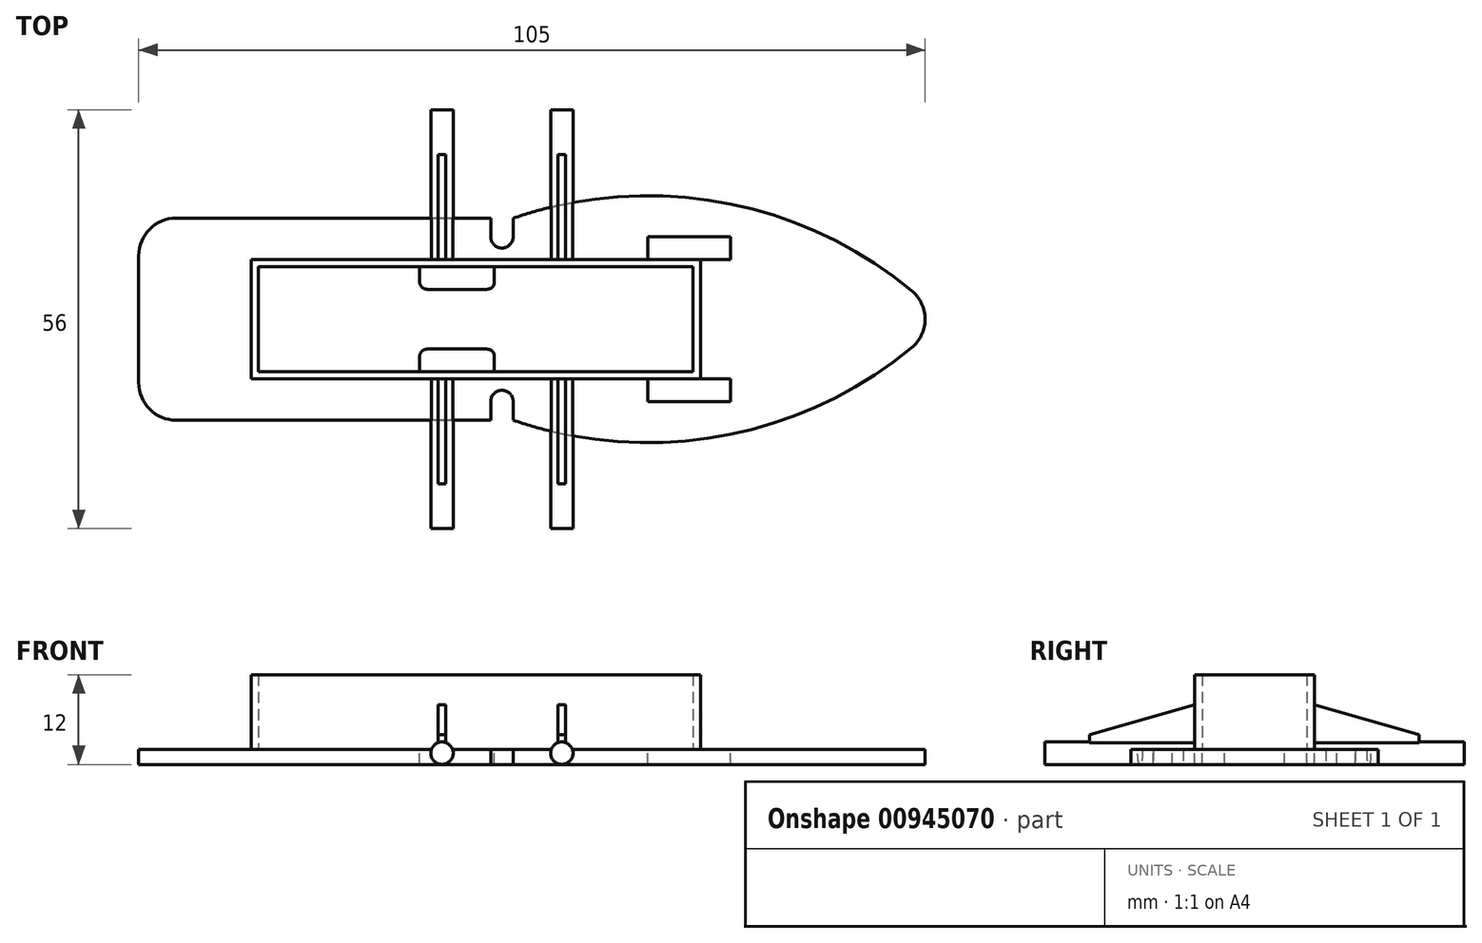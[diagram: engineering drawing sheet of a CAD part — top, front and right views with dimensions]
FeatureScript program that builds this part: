
annotation { "Feature Type Name" : "Feature", "Feature Type Description" : "" }
export const myFeature = defineFeature(function(context is Context, id is Id, definition is map)
    precondition{}
    {
        {
            var Q0;
            Q0=qCreatedBy(makeId("Top.planeOp"),FACE);
            var sketch = newSketch(context, id + "F0", { "sketchPlane" : qUnion([Q0])});
            skLineSegment(sketch, "E0", {"start": v(-48.5, 0) * mm, "end": v(-48.5, 8.5) * mm});
            skLineSegment(sketch, "E1", {"start": v(-43.5, 13.5) * mm, "end": v(-1.5, 13.5) * mm});
            skLineSegment(sketch, "E2", {"start": v(-1.5, 13.5) * mm, "end": v(-1.5, 11) * mm});
            skLineSegment(sketch, "E3", {"start": v(1.5, 11) * mm, "end": v(1.5, 13.5) * mm});
            skArc(sketch, "E4", {"start": v(54.68, 3.86) * mm, "mid": v(29.35, 15.61) * mm, "end": v(1.5, 13.5) * mm});
            skArc(sketch, "E5", {"start": v(-1.5, 11) * mm, "mid": v(0, 9.5) * mm, "end": v(1.5, 11) * mm});
            skPoint(sketch, "E6.visualSharp", {"position": v(-48.5, 13.5) * mm});
            skArc(sketch, "E6.filletArc", {"start": v(-43.5, 13.5) * mm, "mid": v(-47.04, 12.04) * mm, "end": v(-48.5, 8.5) * mm});
            skLineSegment(sketch, "E7.MirrorCS", {"start": v(1.5, -11) * mm, "end": v(1.5, -13.5) * mm});
            skLineSegment(sketch, "E8.MirrorCS", {"start": v(-1.5, -13.5) * mm, "end": v(-1.5, -11) * mm});
            skArc(sketch, "E9.MirrorCS", {"start": v(-43.5, -13.5) * mm, "mid": v(-47.04, -12.04) * mm, "end": v(-48.5, -8.5) * mm});
            skArc(sketch, "E10.MirrorCS", {"start": v(-1.5, -11) * mm, "mid": v(0, -9.5) * mm, "end": v(1.5, -11) * mm});
            skLineSegment(sketch, "E11.MirrorCS", {"start": v(-43.5, -13.5) * mm, "end": v(-1.5, -13.5) * mm});
            skPoint(sketch, "E12.MirrorP", {"position": v(-48.5, -13.5) * mm});
            skArc(sketch, "E13.MirrorCS", {"start": v(54.68, -3.86) * mm, "mid": v(29.35, -15.61) * mm, "end": v(1.5, -13.5) * mm});
            skLineSegment(sketch, "E14.MirrorCS", {"start": v(-48.5, 0) * mm, "end": v(-48.5, -8.5) * mm});
            skPoint(sketch, "E15.visualSharp", {"position": v(58.9, 0) * mm});
            skArc(sketch, "E15.filletArc", {"start": v(54.68, -3.86) * mm, "mid": v(56.5, 0) * mm, "end": v(54.68, 3.86) * mm});
            skSolve(sketch);
        }
        {
            var Q0;
            Q0 = qSketchRegion(id + "F0", true);
            extrude(context, id + "F1", {"entities" : qUnion([Q0]), "depth" : 2 * mm, "offsetDistance" : 25 * mm, "symmetric" : true});
        }
        {
            var Q0;
            Q0=makeQuery(id+"F1.opExtrude","CAP_FACE",FACE,{"disambiguationData":[OSD([sQuery(id+"F0.wireOp",EDGE,"E0"),sQuery(id+"F0.wireOp",EDGE,"E1"),sQuery(id+"F0.wireOp",EDGE,"E2"),sQuery(id+"F0.wireOp",EDGE,"E3"),sQuery(id+"F0.wireOp",EDGE,"E4"),sQuery(id+"F0.wireOp",EDGE,"E5"),sQuery(id+"F0.wireOp",EDGE,"E6.filletArc"),sQuery(id+"F0.wireOp",EDGE,"E7.MirrorCS"),sQuery(id+"F0.wireOp",EDGE,"E8.MirrorCS"),sQuery(id+"F0.wireOp",EDGE,"E9.MirrorCS"),sQuery(id+"F0.wireOp",EDGE,"E10.MirrorCS"),sQuery(id+"F0.wireOp",EDGE,"E11.MirrorCS"),sQuery(id+"F0.wireOp",EDGE,"E13.MirrorCS"),sQuery(id+"F0.wireOp",EDGE,"E14.MirrorCS"),sQuery(id+"F0.wireOp",EDGE,"E15.filletArc")])],"isStart":false});
            var sketch = newSketch(context, id + "F2", { "sketchPlane" : qUnion([Q0])});
            skLineSegment(sketch, "E16", {"start": v(-33.5, 8) * mm, "end": v(26.5, 8) * mm});
            skLineSegment(sketch, "E17.bottom", {"start": v(-33.5, -8) * mm, "end": v(26.5, -8) * mm});
            skLineSegment(sketch, "E17.left", {"start": v(-33.5, -8) * mm, "end": v(-33.5, 8) * mm});
            skLineSegment(sketch, "E17.right", {"start": v(26.5, -8) * mm, "end": v(26.5, 8) * mm});
            skLineSegment(sketch, "E18.0", {"start": v(-32.5, 7) * mm, "end": v(25.5, 7) * mm});
            skLineSegment(sketch, "E18.1", {"start": v(-32.5, -7) * mm, "end": v(-32.5, 7) * mm});
            skLineSegment(sketch, "E18.2", {"start": v(-32.5, -7) * mm, "end": v(25.5, -7) * mm});
            skLineSegment(sketch, "E18.3", {"start": v(25.5, -7) * mm, "end": v(25.5, 7) * mm});
            skSolve(sketch);
        }
        {
            var Q0;
            Q0 = qSketchRegion(id + "F2", true);
            extrude(context, id + "F3", {"entities" : qUnion([Q0]), "operationType" : NewBodyOperationType.ADD, "depth" : 10 * mm, "offsetDistance" : 25 * mm});
        }
        {
            var Q0;
            Q0=makeQuery(id+"F3.opExtrude","SWEPT_FACE",FACE,{"disambiguationData":[OSD([sQuery(id+"F2.wireOp",EDGE,"E17.bottom")])]});
            var sketch = newSketch(context, id + "F4", { "sketchPlane" : qUnion([Q0])});
            skCircle(sketch, "E19", {"center": v(-8, 0.5) * mm, "radius": 1.5 * mm});
            skCircle(sketch, "E20.MirrorC", {"center": v(8, 0.5) * mm, "radius": 1.5 * mm});
            skSolve(sketch);
        }
        {
            var Q0;
            Q0 = qSketchRegion(id + "F4", true);
            extrude(context, id + "F5", {"entities" : qUnion([Q0]), "operationType" : NewBodyOperationType.ADD, "depth" : 20 * mm, "offsetDistance" : 25 * mm});
        }
        {
            var Q0;
            Q0=qCreatedBy(makeId("Right.planeOp"),FACE);
            cPlane(context, id + "F6", {"entities" : qUnion([Q0]), "cplaneType" : CPlaneType.OFFSET, "offset" : 8 * mm, "oppositeDirection" : true, "width" : 150 * mm, "height" : 150 * mm});
        }
        {
            var Q0;
            Q0=qCreatedBy(id+"F6.planeOp",FACE);
            var sketch = newSketch(context, id + "F7", { "sketchPlane" : qUnion([Q0])});
            skLineSegment(sketch, "E21", {"start": v(-22, 3) * mm, "end": v(-8, 7) * mm});
            skLineSegment(sketch, "E22", {"start": v(-22, 3) * mm, "end": v(-22, 0) * mm});
            skLineSegment(sketch, "E23", {"start": v(-8, 7) * mm, "end": v(-8, 0) * mm});
            skLineSegment(sketch, "E24", {"start": v(-8, 0) * mm, "end": v(-22, 0) * mm});
            skSolve(sketch);
        }
        {
            var Q0;
            Q0=makeQuery(id+"F7.imprint","IMPRINT",FACE,{"disambiguationData":[TD([[makeQuery(id+"F7.imprint","IMPRINT",EDGE,{"derivedFrom":sQuery(id+"F7.wireOp",EDGE,"E21")}),-1.0]])]});
            extrude(context, id + "F8", {"entities" : qUnion([Q0]), "depth" : 1 * mm, "offsetDistance" : 25 * mm, "symmetric" : true});
        }
        {
            var Q0;
            Q0=makeQuery(id+"F8.opExtrude","SWEPT_BODY",BODY,{"disambiguationData":[OSD([sQuery(id+"F7.wireOp",EDGE,"E21"),sQuery(id+"F7.wireOp",EDGE,"E22"),sQuery(id+"F7.wireOp",EDGE,"E23"),sQuery(id+"F7.wireOp",EDGE,"E24")])]});
            var Q1;
            Q1=qCreatedBy(makeId("Right.planeOp"),FACE);
            mirror(context, id + "F9", {"operationType" : NewBodyOperationType.ADD, "entities" : qUnion([Q0]), "mirrorPlane" : qUnion([Q1])});
        }
        {
            var Q0;
            Q0=makeQuery(id+"F1.opExtrude","SWEPT_BODY",BODY,{"disambiguationData":[OSD([sQuery(id+"F0.wireOp",EDGE,"E0"),sQuery(id+"F0.wireOp",EDGE,"E1"),sQuery(id+"F0.wireOp",EDGE,"E2"),sQuery(id+"F0.wireOp",EDGE,"E3"),sQuery(id+"F0.wireOp",EDGE,"E4"),sQuery(id+"F0.wireOp",EDGE,"E5"),sQuery(id+"F0.wireOp",EDGE,"E6.filletArc"),sQuery(id+"F0.wireOp",EDGE,"E7.MirrorCS"),sQuery(id+"F0.wireOp",EDGE,"E8.MirrorCS"),sQuery(id+"F0.wireOp",EDGE,"E9.MirrorCS"),sQuery(id+"F0.wireOp",EDGE,"E10.MirrorCS"),sQuery(id+"F0.wireOp",EDGE,"E11.MirrorCS"),sQuery(id+"F0.wireOp",EDGE,"E13.MirrorCS"),sQuery(id+"F0.wireOp",EDGE,"E14.MirrorCS"),sQuery(id+"F0.wireOp",EDGE,"E15.filletArc")])]});
            var Q1;
            Q1=qCreatedBy(makeId("Front.planeOp"),FACE);
            mirror(context, id + "F10", {"operationType" : NewBodyOperationType.ADD, "entities" : qUnion([Q0]), "mirrorPlane" : qUnion([Q1])});
        }
        {
            var Q0;
            {var subQ0=sQuery(id+"F0.wireOp",EDGE,"E9.MirrorCS");var subQ2=sQuery(id+"F0.wireOp",EDGE,"E6.filletArc");var subQ3=makeQuery(id+"F1.opExtrude","SWEPT_FACE",FACE,{"disambiguationData":[OSD([subQ2])]});var subQ4=sQuery(id+"F0.wireOp",EDGE,"E1");var subQ5=makeQuery(id+"F1.opExtrude","SWEPT_FACE",FACE,{"disambiguationData":[OSD([subQ4])]});var subQ7=sQuery(id+"F0.wireOp",EDGE,"E14.MirrorCS");var subQ8=sQuery(id+"F0.wireOp",EDGE,"E0");var subQ10=sQuery(id+"F0.wireOp",EDGE,"E11.MirrorCS");var subQ15=sQuery(id+"F0.wireOp",EDGE,"E5");var subQ17=sQuery(id+"F0.wireOp",EDGE,"E4");var subQ19=sQuery(id+"F0.wireOp",EDGE,"E13.MirrorCS");var subQ21=sQuery(id+"F0.wireOp",EDGE,"E2");var subQ23=sQuery(id+"F0.wireOp",EDGE,"E3");var subQ25=sQuery(id+"F0.wireOp",EDGE,"E15.filletArc");var subQ28=sQuery(id+"F0.wireOp",EDGE,"E8.MirrorCS");var subQ29=sQuery(id+"F0.wireOp",EDGE,"E7.MirrorCS");var subQ30=sQuery(id+"F0.wireOp",EDGE,"E10.MirrorCS");Q0=makeQuery(id+"FKtTZ5iZsvDC3qs_1.boolean.opBoolean","SPLIT",FACE,{"disambiguationData":[TD([subQ3])],"derivedFrom":makeQuery(id+"F5.boolean.opBoolean","SPLIT",FACE,{"disambiguationData":[TD([subQ5])],"derivedFrom":makeQuery(id+"F3.boolean.opBoolean","SPLIT",FACE,{"disambiguationData":[TD([subQ5])],"derivedFrom":makeQuery(id+"F1.opExtrude","CAP_FACE",FACE,{"disambiguationData":[OSD([subQ8,subQ4,subQ21,subQ23,subQ17,subQ15,subQ2,subQ29,subQ28,subQ0,subQ30,subQ10,subQ19,subQ7,subQ25])],"isStart":false})})})});}
            var sketch = newSketch(context, id + "F11", { "sketchPlane" : qUnion([Q0])});
            skLineSegment(sketch, "E25.bottom", {"start": v(19.5, 8) * mm, "end": v(30.5, 8) * mm});
            skLineSegment(sketch, "E25.top", {"start": v(19.5, 11) * mm, "end": v(30.5, 11) * mm});
            skLineSegment(sketch, "E25.left", {"start": v(19.5, 8) * mm, "end": v(19.5, 11) * mm});
            skLineSegment(sketch, "E25.right", {"start": v(30.5, 8) * mm, "end": v(30.5, 11) * mm});
            skLineSegment(sketch, "E26.bottom", {"start": v(-10, 4) * mm, "end": v(-2, 4) * mm});
            skLineSegment(sketch, "E26.top", {"start": v(-11, 7) * mm, "end": v(-1, 7) * mm});
            skLineSegment(sketch, "E26.left", {"start": v(-11, 5) * mm, "end": v(-11, 7) * mm});
            skLineSegment(sketch, "E26.right", {"start": v(-1, 5) * mm, "end": v(-1, 7) * mm});
            skPoint(sketch, "E27.visualSharp", {"position": v(-11, 4) * mm});
            skArc(sketch, "E27.filletArc", {"start": v(-11, 5) * mm, "mid": v(-10.7, 4.3) * mm, "end": v(-10, 4) * mm});
            skPoint(sketch, "E28.visualSharp", {"position": v(-1, 4) * mm});
            skArc(sketch, "E28.filletArc", {"start": v(-2, 4) * mm, "mid": v(-1.3, 4.3) * mm, "end": v(-1, 5) * mm});
            skArc(sketch, "E29.MirrorCS", {"start": v(-11, -5) * mm, "mid": v(-10.7, -4.3) * mm, "end": v(-10, -4) * mm});
            skArc(sketch, "E30.MirrorCS", {"start": v(-2, -4) * mm, "mid": v(-1.3, -4.3) * mm, "end": v(-1, -5) * mm});
            skPoint(sketch, "E31.MirrorP", {"position": v(-1, -4) * mm});
            skLineSegment(sketch, "E32.MirrorCS", {"start": v(-11, -7) * mm, "end": v(-1, -7) * mm});
            skLineSegment(sketch, "E33.MirrorCS", {"start": v(19.5, -8) * mm, "end": v(30.5, -8) * mm});
            skLineSegment(sketch, "E34.MirrorCS", {"start": v(19.5, -8) * mm, "end": v(19.5, -11) * mm});
            skPoint(sketch, "E35.MirrorP", {"position": v(-11, -4) * mm});
            skLineSegment(sketch, "E36.MirrorCS", {"start": v(-11, -5) * mm, "end": v(-11, -7) * mm});
            skLineSegment(sketch, "E37.MirrorCS", {"start": v(30.5, -8) * mm, "end": v(30.5, -11) * mm});
            skLineSegment(sketch, "E38.MirrorCS", {"start": v(19.5, -11) * mm, "end": v(30.5, -11) * mm});
            skLineSegment(sketch, "E39.MirrorCS", {"start": v(-1, -5) * mm, "end": v(-1, -7) * mm});
            skLineSegment(sketch, "E40.MirrorCS", {"start": v(-10, -4) * mm, "end": v(-2, -4) * mm});
            skSolve(sketch);
        }
        {
            var Q0;
            Q0 = qSketchRegion(id + "F11", true);
            extrude(context, id + "F12", {"entities" : qUnion([Q0]), "operationType" : NewBodyOperationType.REMOVE, "endBound" : BoundingType.THROUGH_ALL, "oppositeDirection" : true, "depth" : 25 * mm, "offsetDistance" : 25 * mm});
        }
    });
